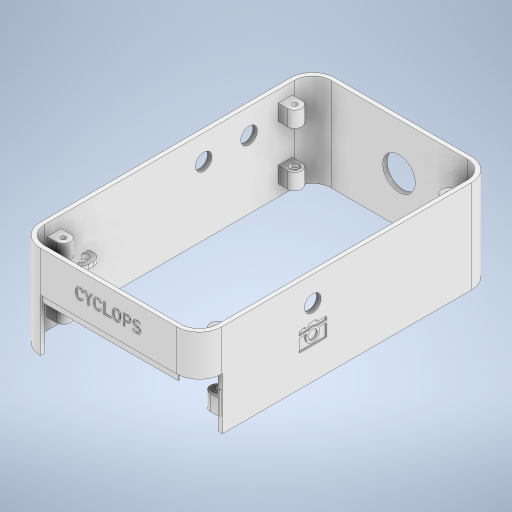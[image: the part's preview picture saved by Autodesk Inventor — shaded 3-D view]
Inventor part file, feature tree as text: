
AUTODESK INVENTOR PART (.ipt)
format: ipt  version: 2023 (Build 270158000, 158)  size: 733,696 bytes
history: native  units: mm
features: sketch x14, extrude x8, hole x3, emboss x3, plane x2, mirror x1
ambient origin geometry x8: Origin, YZ Plane, XZ Plane, XY Plane, X Axis, Y Axis, Z Axis, Center Point
bodies: Solid1 (feature_tree)
feature tree (31):
  extrude  "Extrusion1"  Depth=130.0mm
  plane  "Work Plane1"
  extrude  "Extrusion2"  Depth=1.9mm
  sketch  "Sketch11"  dims[d28=6.0mm d29=4.0mm d30=2.0mm d31=90.0deg d32=14.0mm d33=0.0mm d34=80.0mm]
  extrude  "Extrusion6"  TaperAngle=0.0deg  [1 undecoded]
  mirror  "Mirror1"
  hole  "Hole2"  [1 undecoded]
  hole  "Hole3"  [1 undecoded]
  hole  "Hole4"  [1 undecoded]
  extrude  "Extrusion3"  Depth=10.0mm
  extrude  "Extrusion4"  Depth=7.2mm
  plane  "Work Plane2"
  extrude  "Extrusion5"  Depth=80.0mm
  extrude  "Extrusion7"  Depth=30.0mm
  emboss  "Emboss3"
  emboss  "Emboss1"
  emboss  "Emboss2"
  extrude  "Extrusion24"  Depth=6.0mm
  sketch  "Sketch1"  dims[d0=80.0mm d1=130.0mm]
  sketch  "Sketch2"  dims[d2=10.0mm d3=1.9mm]
  sketch  "Sketch4"  dims[d4=41.0mm d5=0.0mm]
  sketch  "Sketch5"  dims[d6=-5.1mm d7=2.2mm]
  sketch  "Sketch6"  dims[d8=14.0mm d9=6.0mm]
  sketch  "Sketch7"  dims[d10=2.0mm d11=20.0mm d13=102.0mm]
  sketch  "Sketch8"  dims[d14=10.0mm d16=10.0mm d18=7.0mm]
  sketch  "Sketch10"  dims[d19=0.0mm d27=7.2mm]
  sketch  "Sketch12"  dims[d35=100.0mm d36=30.0mm]
  sketch  "Sketch13"  dims[d37=7.2mm]
  sketch  "Sketch14"  dims[d38=6.0mm d39=4.0mm d40=2.0mm d41=90.0deg d42=8.0mm d43=0.0mm d44=50.0mm]
  sketch  "Sketch15"  dims[d45=30.0mm]
  sketch  "Sketch34"  dims[d46=14.3mm d47=6.0mm d48=4.0mm d49=2.0mm d50=90.0deg d51=8.0mm d52=0.0mm d53=70.0mm d55=10.2mm d56=0.0mm d57=23.0mm d58=0.5mm d59=3.0mm d60=60.0mm d61=0.0mm d62=-11.5mm d63=0.5mm d65=0.25mm d66=10.0mm d67=0.0mm d68=1.9mm d69=20.0mm d71=68.0mm d72=20.0mm d74=102.0mm d77=1.7mm d78=0.0mm d83=2.0mm d84=0.0mm d85=2.0mm d88=3.3mm d89=25.0mm d90=4.363323mm d91=5.3mm d92=12.0mm d93=4.0mm d94=6.0mm d95=12.0mm d96=8.0mm d97=3.0mm d98=120.0deg d99=1.0mm d100=1.5mm d101=1.0mm d102=1.5mm d103=1.0mm d104=3.0mm d105=3.0mm d106=120.0deg d108=4.0mm d110=1.5mm d111=0.5mm d112=1.0mm d113=120.0deg d114=0.5mm d115=0.0mm d116=12.0mm d117=9.0mm d118=1.3mm d119=12.0mm d120=9.0mm d121=1.3mm d122=6.0mm d123=0.5mm d124=0.0mm d125=0.5mm d126=0.0mm d127=30.0mm d128=5.5mm d169=25.0mm d170=0.0mm d139=0.5mm d140=0.872665mm d141=0.5mm d142=0.872665mm d147=0.5mm d148=0.872665mm d149=0.5mm d150=0.872665mm d167=0.5mm d168=0.872665mm d171=0.5mm d172=0.872665mm]
note: 4 required parameter values undecoded (feature->parameter linkage not recoverable at this tier; creation-order binding heuristic only, values carry confidence <= 0.55)
